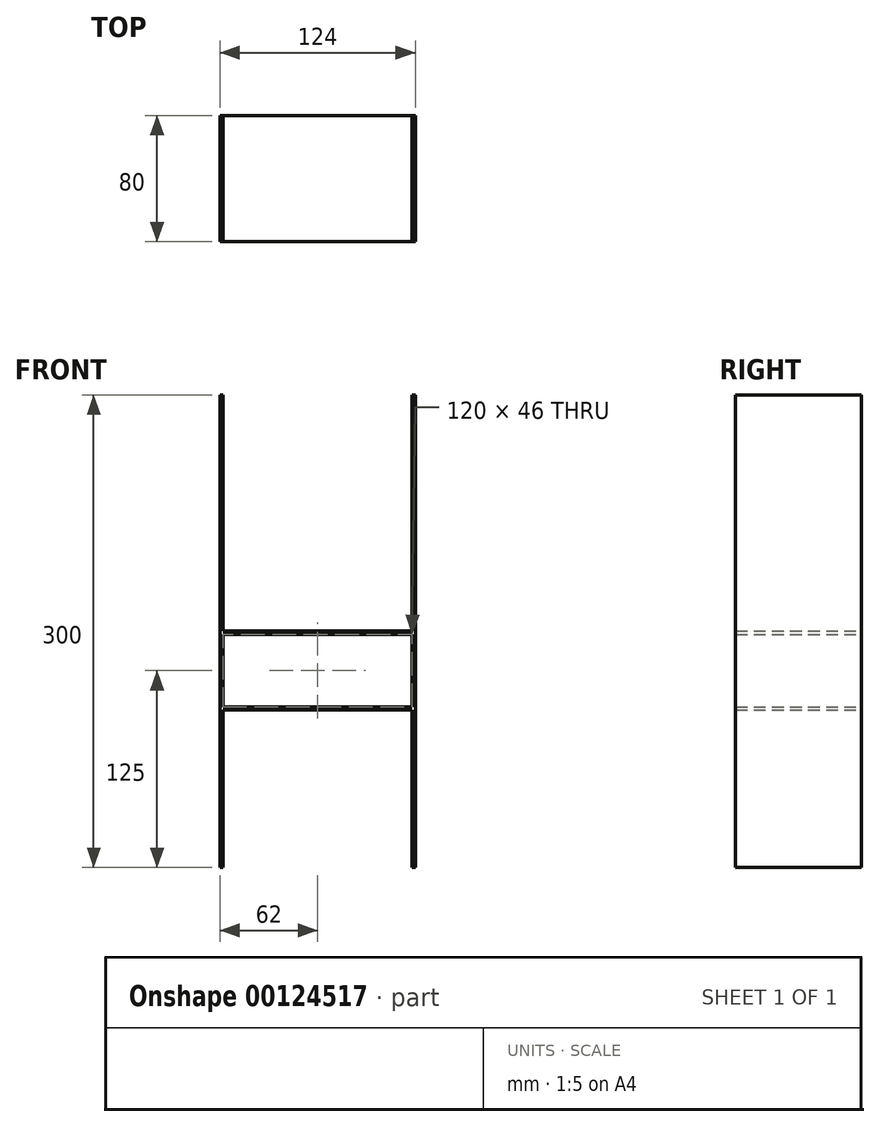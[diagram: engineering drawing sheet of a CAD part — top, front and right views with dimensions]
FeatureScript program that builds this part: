
annotation { "Feature Type Name" : "Feature", "Feature Type Description" : "" }
export const myFeature = defineFeature(function(context is Context, id is Id, definition is map)
    precondition{}
    {
        {
            var Q0;
            Q0=qCreatedBy(makeId("Front.planeOp"),FACE);
            var sketch = newSketch(context, id + "F0", { "sketchPlane" : qUnion([Q0])});
            skLineSegment(sketch, "E0", {"start": v(0, -55.06) * mm, "end": v(0, 55.06) * mm, "construction": true});
            skLineSegment(sketch, "E1", {"start": v(-60, 0) * mm, "end": v(60, 0) * mm});
            skLineSegment(sketch, "E2", {"start": v(60, 0) * mm, "end": v(60, 150) * mm});
            skLineSegment(sketch, "E3", {"start": v(60, 150) * mm, "end": v(62, 150) * mm});
            skLineSegment(sketch, "E4", {"start": v(62, 150) * mm, "end": v(62, -150) * mm});
            skLineSegment(sketch, "E5", {"start": v(62, -150) * mm, "end": v(60, -150) * mm});
            skLineSegment(sketch, "E6", {"start": v(60, -150) * mm, "end": v(60, -50) * mm});
            skLineSegment(sketch, "E7", {"start": v(60, -50) * mm, "end": v(-60, -50) * mm});
            skLineSegment(sketch, "E8", {"start": v(-60, -50) * mm, "end": v(-60, -150) * mm});
            skLineSegment(sketch, "E9", {"start": v(-60, -150) * mm, "end": v(-62, -150) * mm});
            skLineSegment(sketch, "E10", {"start": v(60, -2) * mm, "end": v(-60, -2) * mm});
            skLineSegment(sketch, "E11", {"start": v(-60, -2) * mm, "end": v(-60, -48) * mm});
            skLineSegment(sketch, "E12", {"start": v(-60, -48) * mm, "end": v(60, -48) * mm});
            skLineSegment(sketch, "E13", {"start": v(60, -48) * mm, "end": v(60, -2) * mm});
            skLineSegment(sketch, "E14", {"start": v(-62, -150) * mm, "end": v(-62, 150) * mm});
            skLineSegment(sketch, "E15", {"start": v(-62, 150) * mm, "end": v(-60, 150) * mm});
            skLineSegment(sketch, "E16", {"start": v(-60, 150) * mm, "end": v(-60, 0) * mm});
            skSolve(sketch);
        }
        {
            var Q0;
            Q0 = qSketchRegion(id + "F0", true);
            extrude(context, id + "F1", {"entities" : qUnion([Q0]), "endBound" : BoundingType.SYMMETRIC, "depth" : 80 * mm});
        }
    });
